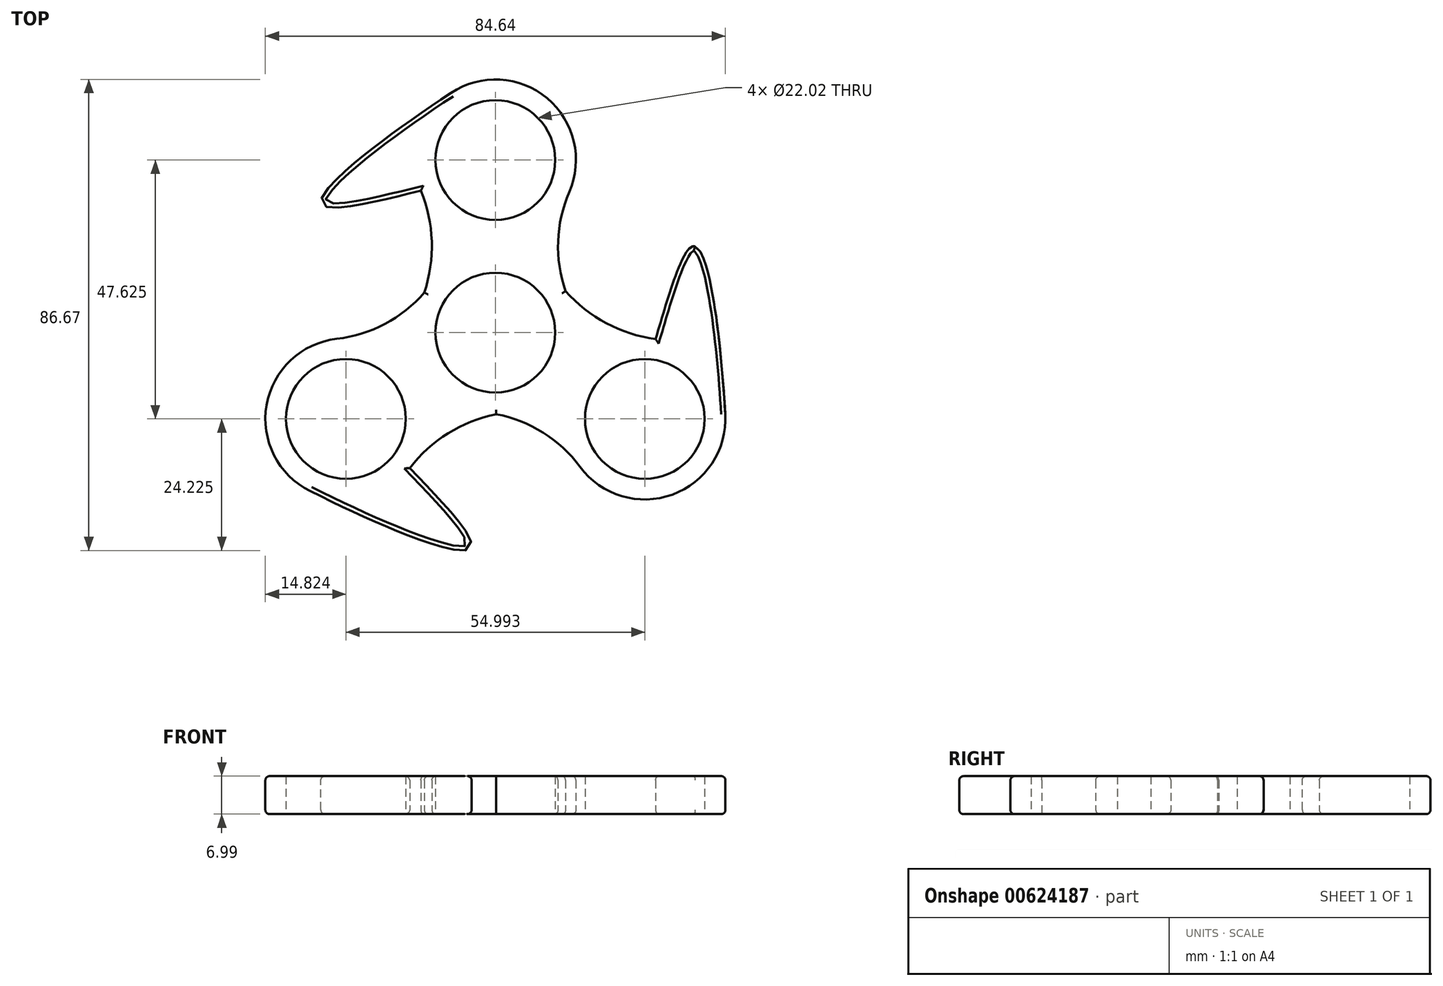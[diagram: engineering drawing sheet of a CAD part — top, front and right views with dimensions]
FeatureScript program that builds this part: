
annotation { "Feature Type Name" : "Feature", "Feature Type Description" : "" }
export const myFeature = defineFeature(function(context is Context, id is Id, definition is map)
    precondition{}
    {
        {
            var Q0;
            Q0=qCreatedBy(makeId("Top.planeOp"),FACE);
            var sketch = newSketch(context, id + "F0", { "sketchPlane" : qUnion([Q0])});
            skCircle(sketch, "E0", {"center": v(0, 0) * mm, "radius": 11.01 * mm});
            skLineSegment(sketch, "E1", {"start": v(0, 0) * mm, "end": v(0, 31.75) * mm});
            skCircle(sketch, "E2", {"center": v(0, 31.75) * mm, "radius": 11.01 * mm});
            skCircle(sketch, "E3", {"center": v(0, 31.75) * mm, "radius": 14.82 * mm});
            skCircle(sketch, "E4", {"center": v(0, 0) * mm, "radius": 14.82 * mm});
            skArc(sketch, "E5", {"start": v(-13.71, 5.63) * mm, "mid": v(-11.69, 15.88) * mm, "end": v(-13.71, 26.12) * mm});
            skArc(sketch, "E6", {"start": v(13.6, 25.85) * mm, "mid": v(11.52, 15.88) * mm, "end": v(13.6, 5.9) * mm});
            skArc(sketch, "E7.1.0", {"start": v(1.98, -14.69) * mm, "mid": v(-7.9, -18.06) * mm, "end": v(-15.77, -24.93) * mm});
            skCircle(sketch, "E7.1.1", {"center": v(-27.5, -15.88) * mm, "radius": 14.82 * mm});
            skCircle(sketch, "E7.1.2", {"center": v(-27.5, -15.88) * mm, "radius": 11.01 * mm});
            skLineSegment(sketch, "E7.1.3", {"start": v(0, 0) * mm, "end": v(-27.5, -15.87) * mm});
            skArc(sketch, "E7.1.4", {"start": v(-29.18, -1.15) * mm, "mid": v(-19.5, 2.04) * mm, "end": v(-11.9, 8.82) * mm});
            skArc(sketch, "E7.2.0", {"start": v(11.73, 9.06) * mm, "mid": v(19.6, 2.19) * mm, "end": v(29.48, -1.19) * mm});
            skCircle(sketch, "E7.2.1", {"center": v(27.5, -15.88) * mm, "radius": 14.82 * mm});
            skCircle(sketch, "E7.2.2", {"center": v(27.5, -15.88) * mm, "radius": 11.01 * mm});
            skLineSegment(sketch, "E7.2.3", {"start": v(0, 0) * mm, "end": v(27.5, -15.87) * mm});
            skArc(sketch, "E7.2.4", {"start": v(15.59, -24.7) * mm, "mid": v(7.99, -17.92) * mm, "end": v(-1.69, -14.72) * mm});
            skFitSpline(sketch, "E8", {"points": [v(-15.77, -24.93) * mm, v(-4.53, -39.6) * mm, v(-34.12, -29.13) * mm], "startDerivative": vector(43.9, -45.45) * mm, "endDerivative": vector(-74.69, 37.32) * mm});
            skFitSpline(sketch, "E9", {"points": [v(29.48, -1.19) * mm, v(36.57, 15.88) * mm, v(42.3, -15) * mm], "startDerivative": vector(18.1, 60.55) * mm, "endDerivative": vector(4.9, -83.48) * mm});
            skFitSpline(sketch, "E10", {"points": [v(-13.71, 26.12) * mm, v(-32.03, 23.73) * mm, v(-8.17, 44.12) * mm], "startDerivative": vector(-61.3, -15.29) * mm, "endDerivative": vector(69.67, 46.02) * mm});
            skSolve(sketch);
        }
        {
            var Q0;
            Q0 = qSketchRegion(id + "F0", true);
            var Q1;
            {var subQ0=sQuery(id+"F0.wireOp",EDGE,"E4");var subQ7=makeQuery(id+"F0.imprint","IMPRINT",VERTEX,{"derivedFrom":subQ0});Q1=makeQuery(id+"F0.imprint","IMPRINT",FACE,{"disambiguationData":[TD([[makeQuery(id+"F0.imprint","IMPRINT",EDGE,{"disambiguationData":[TD([[subQ7,1.0]])],"derivedFrom":subQ0}),1.0]])]});}
            var Q2;
            {var subQ5=sQuery(id+"F0.wireOp",EDGE,"E7.1.3");var subQ7=sQuery(id+"F0.wireOp",EDGE,"E0");var subQ8=makeQuery(id+"F0.imprint","INTERSECT",VERTEX,{"derivedFrom":[subQ7,subQ5]});Q2=makeQuery(id+"F0.imprint","IMPRINT",FACE,{"disambiguationData":[TD([[makeQuery(id+"F0.imprint","IMPRINT",EDGE,{"disambiguationData":[TD([[subQ8,-1.0]])],"derivedFrom":subQ7}),-1.0]])]});}
            var Q3;
            {var subQ4=sQuery(id+"F0.wireOp",EDGE,"E1");var subQ6=sQuery(id+"F0.wireOp",EDGE,"E0");var subQ7=makeQuery(id+"F0.imprint","INTERSECT",VERTEX,{"derivedFrom":[subQ6,subQ4]});Q3=makeQuery(id+"F0.imprint","IMPRINT",FACE,{"disambiguationData":[TD([[makeQuery(id+"F0.imprint","IMPRINT",EDGE,{"disambiguationData":[TD([[subQ7,1.0]])],"derivedFrom":subQ6}),-1.0]])]});}
            var Q4;
            {var subQ5=sQuery(id+"F0.wireOp",EDGE,"E0");var subQ7=sQuery(id+"F0.wireOp",EDGE,"E7.1.3");var subQ9=makeQuery(id+"F0.imprint","INTERSECT",VERTEX,{"derivedFrom":[subQ5,subQ7]});Q4=makeQuery(id+"F0.imprint","IMPRINT",FACE,{"disambiguationData":[TD([[makeQuery(id+"F0.imprint","IMPRINT",EDGE,{"disambiguationData":[TD([[subQ9,1.0]])],"derivedFrom":subQ5}),-1.0]])]});}
            extrude(context, id + "F1", {"entities" : qUnion([Q0, Q1, Q2, Q3, Q4]), "depth" : 7 * mm, "offsetDistance" : 25.4 * mm});
        }
        {
            var Q0;
            Q0=makeQuery(id+"F1.opExtrude","CAP_EDGE",EDGE,{"disambiguationData":[OSD([sQuery(id+"F0.wireOp",EDGE,"E10")])],"isStart":false});
            var Q1;
            Q1=makeQuery(id+"F1.opExtrude","CAP_EDGE",EDGE,{"disambiguationData":[OSD([sQuery(id+"F0.wireOp",EDGE,"E6")])],"isStart":false});
            var Q2;
            Q2=makeQuery(id+"F1.opExtrude","CAP_EDGE",EDGE,{"disambiguationData":[OSD([sQuery(id+"F0.wireOp",EDGE,"E3")])],"isStart":false});
            var Q3;
            Q3=makeQuery(id+"F1.opExtrude","CAP_EDGE",EDGE,{"disambiguationData":[OSD([sQuery(id+"F0.wireOp",EDGE,"E5")])],"isStart":false});
            var Q4;
            Q4=makeQuery(id+"F1.opExtrude","CAP_EDGE",EDGE,{"disambiguationData":[OSD([sQuery(id+"F0.wireOp",EDGE,"E7.1.4")])],"isStart":false});
            var Q5;
            Q5=makeQuery(id+"F1.opExtrude","CAP_EDGE",EDGE,{"disambiguationData":[OSD([sQuery(id+"F0.wireOp",EDGE,"E7.1.1")])],"isStart":false});
            var Q6;
            Q6=makeQuery(id+"F1.opExtrude","CAP_EDGE",EDGE,{"disambiguationData":[OSD([sQuery(id+"F0.wireOp",EDGE,"E7.1.0")])],"isStart":false});
            var Q7;
            Q7=makeQuery(id+"F1.opExtrude","CAP_EDGE",EDGE,{"disambiguationData":[OSD([sQuery(id+"F0.wireOp",EDGE,"E7.2.4")])],"isStart":false});
            var Q8;
            Q8=makeQuery(id+"F1.opExtrude","CAP_EDGE",EDGE,{"disambiguationData":[OSD([sQuery(id+"F0.wireOp",EDGE,"E7.2.1")])],"isStart":false});
            var Q9;
            Q9=makeQuery(id+"F1.opExtrude","CAP_EDGE",EDGE,{"disambiguationData":[OSD([sQuery(id+"F0.wireOp",EDGE,"E9")])],"isStart":false});
            var Q10;
            Q10=makeQuery(id+"F1.opExtrude","CAP_EDGE",EDGE,{"disambiguationData":[OSD([sQuery(id+"F0.wireOp",EDGE,"E7.2.0")])],"isStart":false});
            var Q11;
            Q11=makeQuery(id+"F1.opExtrude","CAP_EDGE",EDGE,{"disambiguationData":[OSD([sQuery(id+"F0.wireOp",EDGE,"E8")])],"isStart":false});
            fillet(context, id + "F2", {"entities" : qUnion([Q0, Q1, Q2, Q3, Q4, Q5, Q6, Q7, Q8, Q9, Q10, Q11]), "radius" : 0.76 * mm, "tangentPropagation" : true, "allowEdgeOverflow" : false});
        }
        {
            var Q0;
            Q0=makeQuery(id+"F1.opExtrude","CAP_EDGE",EDGE,{"disambiguationData":[OSD([sQuery(id+"F0.wireOp",EDGE,"E8")])],"isStart":true});
            var Q1;
            Q1=makeQuery(id+"F1.opExtrude","CAP_EDGE",EDGE,{"disambiguationData":[OSD([sQuery(id+"F0.wireOp",EDGE,"E7.1.0")])],"isStart":true});
            var Q2;
            Q2=makeQuery(id+"F1.opExtrude","CAP_EDGE",EDGE,{"disambiguationData":[OSD([sQuery(id+"F0.wireOp",EDGE,"E7.2.4")])],"isStart":true});
            var Q3;
            Q3=makeQuery(id+"F1.opExtrude","CAP_EDGE",EDGE,{"disambiguationData":[OSD([sQuery(id+"F0.wireOp",EDGE,"E7.2.1")])],"isStart":true});
            var Q4;
            Q4=makeQuery(id+"F1.opExtrude","CAP_EDGE",EDGE,{"disambiguationData":[OSD([sQuery(id+"F0.wireOp",EDGE,"E7.2.0")])],"isStart":true});
            var Q5;
            Q5=makeQuery(id+"F1.opExtrude","CAP_EDGE",EDGE,{"disambiguationData":[OSD([sQuery(id+"F0.wireOp",EDGE,"E6")])],"isStart":true});
            var Q6;
            Q6=makeQuery(id+"F1.opExtrude","CAP_EDGE",EDGE,{"disambiguationData":[OSD([sQuery(id+"F0.wireOp",EDGE,"E3")])],"isStart":true});
            var Q7;
            Q7=makeQuery(id+"F1.opExtrude","CAP_EDGE",EDGE,{"disambiguationData":[OSD([sQuery(id+"F0.wireOp",EDGE,"E10")])],"isStart":true});
            var Q8;
            Q8=makeQuery(id+"F1.opExtrude","CAP_EDGE",EDGE,{"disambiguationData":[OSD([sQuery(id+"F0.wireOp",EDGE,"E5")])],"isStart":true});
            var Q9;
            Q9=makeQuery(id+"F1.opExtrude","CAP_EDGE",EDGE,{"disambiguationData":[OSD([sQuery(id+"F0.wireOp",EDGE,"E9")])],"isStart":true});
            var Q10;
            Q10=makeQuery(id+"F1.opExtrude","CAP_EDGE",EDGE,{"disambiguationData":[OSD([sQuery(id+"F0.wireOp",EDGE,"E7.1.4")])],"isStart":true});
            var Q11;
            Q11=makeQuery(id+"F1.opExtrude","CAP_EDGE",EDGE,{"disambiguationData":[OSD([sQuery(id+"F0.wireOp",EDGE,"E7.1.1")])],"isStart":true});
            fillet(context, id + "F3", {"entities" : qUnion([Q0, Q1, Q2, Q3, Q4, Q5, Q6, Q7, Q8, Q9, Q10, Q11]), "radius" : 0.76 * mm, "tangentPropagation" : true, "allowEdgeOverflow" : false});
        }
    });
